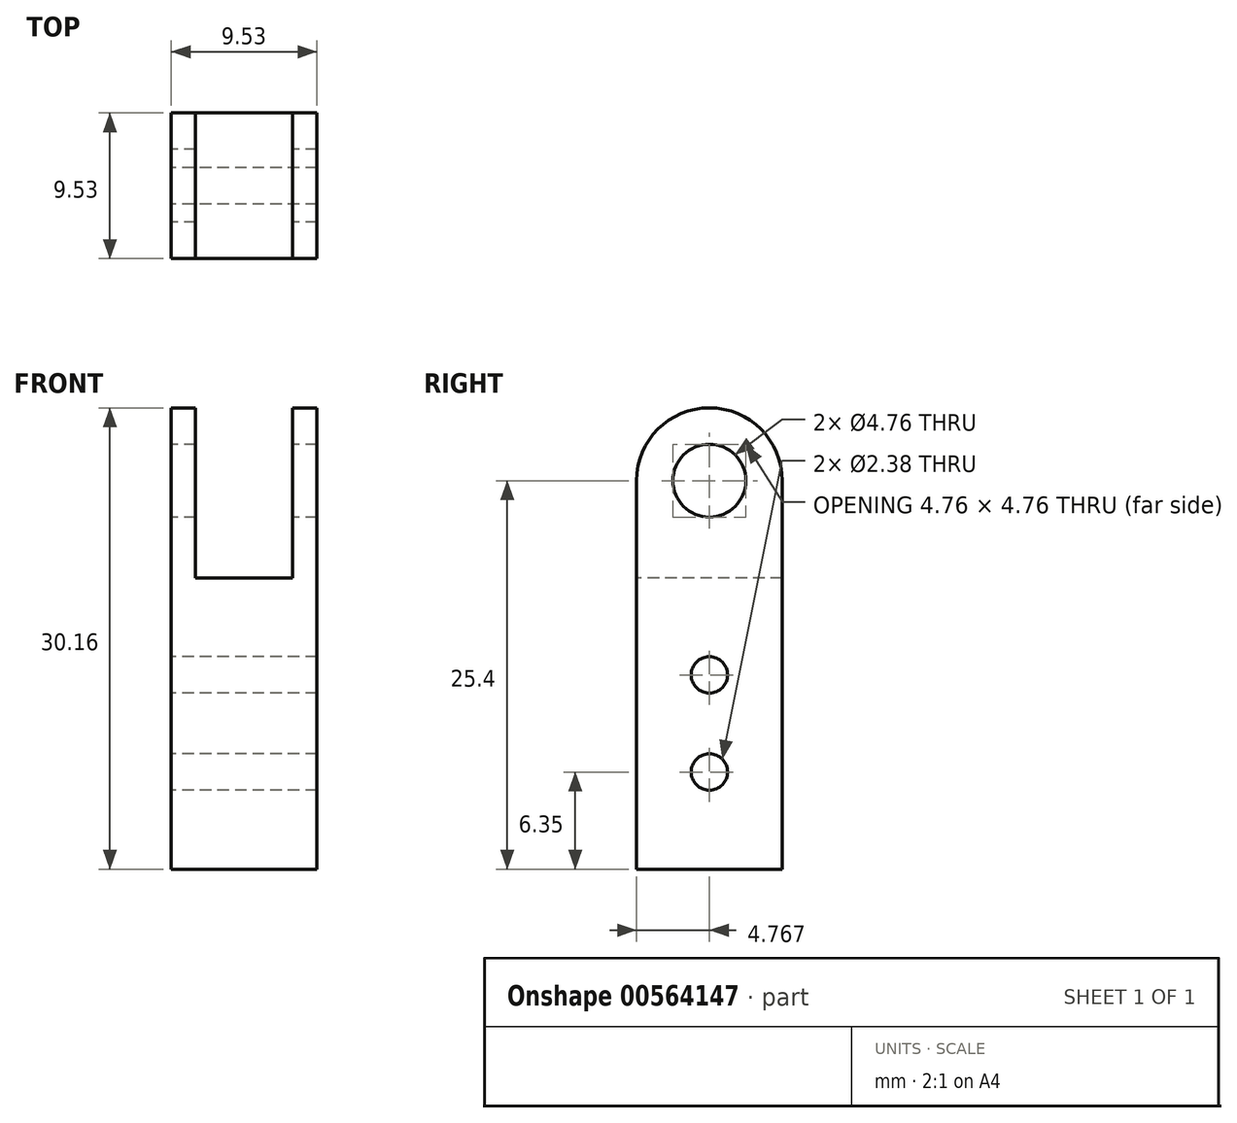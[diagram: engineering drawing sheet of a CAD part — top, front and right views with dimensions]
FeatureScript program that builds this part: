
annotation { "Feature Type Name" : "Feature", "Feature Type Description" : "" }
export const myFeature = defineFeature(function(context is Context, id is Id, definition is map)
    precondition{}
    {
        {
            var Q0;
            Q0=qCreatedBy(makeId("Right.planeOp"),FACE);
            var sketch = newSketch(context, id + "F0", { "sketchPlane" : qUnion([Q0])});
            skLineSegment(sketch, "E0.bottom", {"start": v(0, 0) * mm, "end": v(-9.53, 0) * mm});
            skLineSegment(sketch, "E0.top", {"start": v(0, 25.4) * mm, "end": v(-9.53, 25.4) * mm});
            skLineSegment(sketch, "E0.left", {"start": v(0, 0) * mm, "end": v(0, 25.4) * mm});
            skLineSegment(sketch, "E0.right", {"start": v(-9.53, 0) * mm, "end": v(-9.53, 25.4) * mm});
            skCircle(sketch, "E1", {"center": v(-4.76, 25.4) * mm, "radius": 4.76 * mm});
            skCircle(sketch, "E2", {"center": v(-4.76, 25.4) * mm, "radius": 2.38 * mm});
            skCircle(sketch, "E3", {"center": v(-4.76, 6.35) * mm, "radius": 1.2 * mm});
            skPoint(sketch, "E3.centerSnap0", {"position": v(-4.76, 0) * mm});
            skCircle(sketch, "E4", {"center": v(-4.76, 12.7) * mm, "radius": 1.2 * mm});
            skLineSegment(sketch, "E5", {"start": v(-9.53, 19.05) * mm, "end": v(0, 19.05) * mm});
            skSolve(sketch);
        }
        {
            var Q0;
            Q0 = qSketchRegion(id + "F0", true);
            extrude(context, id + "F1", {"entities" : qUnion([Q0]), "depth" : 9.52 * mm, "offsetDistance" : 25.4 * mm});
        }
        {
            var Q0;
            Q0=makeQuery(id+"F1.opExtrude","SWEPT_FACE",FACE,{"disambiguationData":[OSD([sQuery(id+"F0.wireOp",EDGE,"E0.right")])]});
            var sketch = newSketch(context, id + "F2", { "sketchPlane" : qUnion([Q0])});
            skLineSegment(sketch, "E6.bottom", {"start": v(7.94, 31.75) * mm, "end": v(1.59, 31.75) * mm});
            skLineSegment(sketch, "E6.top", {"start": v(7.94, 19.05) * mm, "end": v(1.59, 19.05) * mm});
            skLineSegment(sketch, "E6.left", {"start": v(7.94, 31.75) * mm, "end": v(7.94, 19.05) * mm});
            skLineSegment(sketch, "E6.right", {"start": v(1.59, 31.75) * mm, "end": v(1.59, 19.05) * mm});
            skPoint(sketch, "E6.middle", {"position": v(4.76, 25.4) * mm});
            skPoint(sketch, "E6.middle.positionSnap0", {"position": v(4.76, 25.4) * mm});
            skPoint(sketch, "E6.centerSnap0", {"position": v(4.76, 25.4) * mm});
            skSolve(sketch);
        }
        {
            var Q0;
            Q0 = qSketchRegion(id + "F2", true);
            extrude(context, id + "F3", {"entities" : qUnion([Q0]), "operationType" : NewBodyOperationType.REMOVE, "endBound" : BoundingType.THROUGH_ALL, "oppositeDirection" : true, "depth" : 25.4 * mm, "offsetDistance" : 25.4 * mm});
        }
    });
